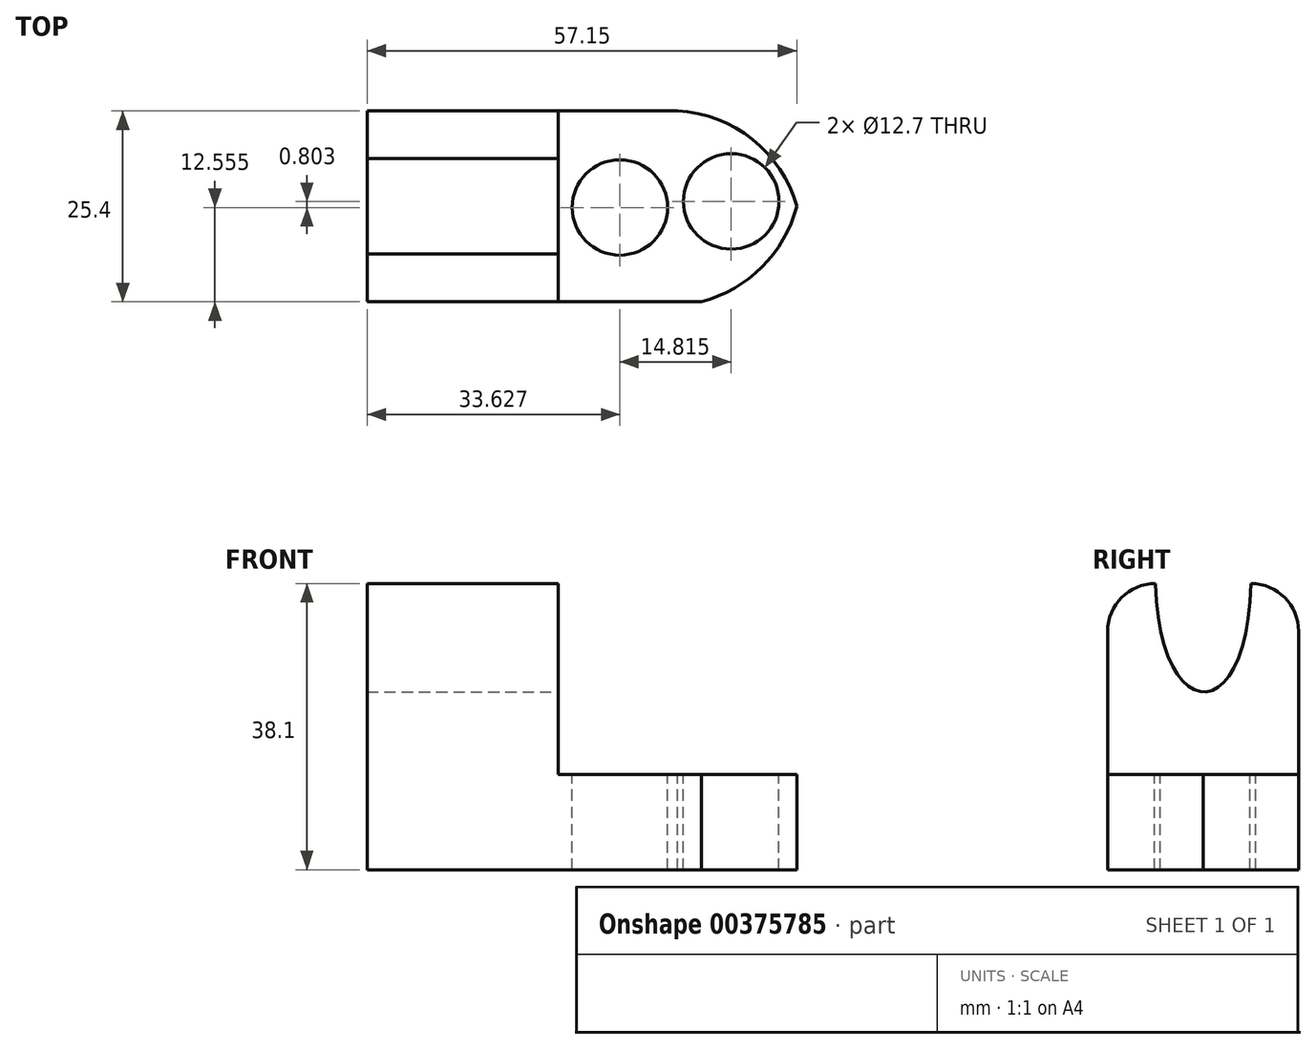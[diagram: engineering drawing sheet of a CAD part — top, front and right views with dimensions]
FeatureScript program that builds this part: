
annotation { "Feature Type Name" : "Feature", "Feature Type Description" : "" }
export const myFeature = defineFeature(function(context is Context, id is Id, definition is map)
    precondition{}
    {
        {
            var Q0;
            Q0=qCreatedBy(makeId("Front.planeOp"),FACE);
            var sketch = newSketch(context, id + "F0", { "sketchPlane" : qUnion([Q0])});
            skLineSegment(sketch, "E0", {"start": v(-57.15, 38.1) * mm, "end": v(-57.15, 0) * mm});
            skLineSegment(sketch, "E1", {"start": v(-57.15, 0) * mm, "end": v(0, 0) * mm});
            skLineSegment(sketch, "E2", {"start": v(0, 0) * mm, "end": v(0, 12.7) * mm});
            skLineSegment(sketch, "E3", {"start": v(0, 12.7) * mm, "end": v(-31.75, 12.7) * mm});
            skLineSegment(sketch, "E4", {"start": v(-31.75, 12.7) * mm, "end": v(-31.75, 38.1) * mm});
            skLineSegment(sketch, "E5", {"start": v(-31.75, 38.1) * mm, "end": v(-57.15, 38.1) * mm});
            skSolve(sketch);
        }
        {
            var Q0;
            Q0=makeQuery(id+"F0.imprint","IMPRINT",FACE,{"disambiguationData":[TD([[makeQuery(id+"F0.imprint","IMPRINT",EDGE,{"derivedFrom":sQuery(id+"F0.wireOp",EDGE,"E0")}),1.0]])]});
            extrude(context, id + "F1", {"entities" : qUnion([Q0]), "depth" : 25.4 * mm});
        }
        {
            var Q0;
            Q0=makeQuery(id+"F1.opExtrude","SWEPT_FACE",FACE,{"disambiguationData":[OSD([sQuery(id+"F0.wireOp",EDGE,"E4")])]});
            var sketch = newSketch(context, id + "F2", { "sketchPlane" : qUnion([Q0])});
            skFitSpline(sketch, "E6", {"points": [v(-19.05, 38.1) * mm, v(-6.35, 38.1) * mm], "startDerivative": vector(1.44, -56.27) * mm, "endDerivative": vector(1.38, 59.05) * mm});
            skLineSegment(sketch, "E7", {"start": v(-19.05, 38.1) * mm, "end": v(-6.35, 38.1) * mm});
            skSolve(sketch);
        }
        {
            var Q0;
            Q0=makeQuery(id+"F2.imprint","IMPRINT",FACE,{"disambiguationData":[TD([[makeQuery(id+"F2.imprint","IMPRINT",EDGE,{"derivedFrom":sQuery(id+"F2.wireOp",EDGE,"E6")}),1.0]])]});
            extrude(context, id + "F3", {"entities" : qUnion([Q0]), "operationType" : NewBodyOperationType.REMOVE, "oppositeDirection" : true, "depth" : 25.4 * mm});
        }
        {
            var Q0;
            Q0=makeQuery(id+"F1.opExtrude","SWEPT_FACE",FACE,{"disambiguationData":[OSD([sQuery(id+"F0.wireOp",EDGE,"E3")])]});
            var sketch = newSketch(context, id + "F4", { "sketchPlane" : qUnion([Q0])});
            skArc(sketch, "E8", {"start": v(0, -12.7) * mm, "mid": v(-5.89, -3.79) * mm, "end": v(-15.88, 0) * mm});
            skArc(sketch, "E9", {"start": v(-12.7, -25.4) * mm, "mid": v(-4.63, -20.77) * mm, "end": v(0, -12.7) * mm});
            skLineSegment(sketch, "E10", {"start": v(-15.88, 0) * mm, "end": v(0, 0) * mm});
            skLineSegment(sketch, "E11", {"start": v(0, 0) * mm, "end": v(0, -12.7) * mm});
            skLineSegment(sketch, "E12", {"start": v(-12.7, -25.4) * mm, "end": v(0, -25.4) * mm});
            skLineSegment(sketch, "E13", {"start": v(0, -25.4) * mm, "end": v(0, -12.7) * mm});
            skSolve(sketch);
        }
        {
            var Q0;
            Q0=makeQuery(id+"F4.imprint","IMPRINT",FACE,{"disambiguationData":[TD([[makeQuery(id+"F4.imprint","IMPRINT",EDGE,{"derivedFrom":sQuery(id+"F4.wireOp",EDGE,"E9")}),-1.0]])]});
            var Q1;
            Q1=makeQuery(id+"F4.imprint","IMPRINT",FACE,{"disambiguationData":[TD([[makeQuery(id+"F4.imprint","IMPRINT",EDGE,{"derivedFrom":sQuery(id+"F4.wireOp",EDGE,"E8")}),-1.0]])]});
            extrude(context, id + "F5", {"entities" : qUnion([Q0, Q1]), "operationType" : NewBodyOperationType.REMOVE, "oppositeDirection" : true, "depth" : 25.4 * mm});
        }
        {
            var Q0;
            Q0=makeQuery(id+"F1.opExtrude","SWEPT_FACE",FACE,{"disambiguationData":[OSD([sQuery(id+"F0.wireOp",EDGE,"E3")])]});
            var sketch = newSketch(context, id + "F6", { "sketchPlane" : qUnion([Q0])});
            skCircle(sketch, "E14", {"center": v(-23.52, -12.84) * mm, "radius": 6.35 * mm});
            skCircle(sketch, "E15", {"center": v(-8.7, -12.04) * mm, "radius": 6.35 * mm});
            skSolve(sketch);
        }
        {
            var Q0;
            Q0=makeQuery(id+"F6.imprint","IMPRINT",FACE,{"disambiguationData":[TD([[makeQuery(id+"F6.imprint","IMPRINT",EDGE,{"derivedFrom":sQuery(id+"F6.wireOp",EDGE,"E14")}),1.0]])]});
            var Q1;
            Q1=makeQuery(id+"F6.imprint","IMPRINT",FACE,{"disambiguationData":[TD([[makeQuery(id+"F6.imprint","IMPRINT",EDGE,{"derivedFrom":sQuery(id+"F6.wireOp",EDGE,"E15")}),1.0]])]});
            extrude(context, id + "F7", {"entities" : qUnion([Q0, Q1]), "operationType" : NewBodyOperationType.REMOVE, "oppositeDirection" : true, "depth" : 25.4 * mm});
        }
        {
            var Q0;
            Q0=makeQuery(id+"F1.opExtrude","SWEPT_FACE",FACE,{"disambiguationData":[OSD([sQuery(id+"F0.wireOp",EDGE,"E0")])]});
            var sketch = newSketch(context, id + "F8", { "sketchPlane" : qUnion([Q0])});
            skArc(sketch, "E16", {"start": v(6.35, 38.1) * mm, "mid": v(1.86, 36.24) * mm, "end": v(0, 31.75) * mm});
            skArc(sketch, "E17", {"start": v(25.4, 31.75) * mm, "mid": v(23.54, 36.24) * mm, "end": v(19.05, 38.1) * mm});
            skLineSegment(sketch, "E18", {"start": v(0, 31.75) * mm, "end": v(0, 38.1) * mm});
            skLineSegment(sketch, "E19", {"start": v(0, 38.1) * mm, "end": v(6.35, 38.1) * mm});
            skLineSegment(sketch, "E20", {"start": v(19.05, 38.1) * mm, "end": v(25.4, 38.1) * mm});
            skLineSegment(sketch, "E21", {"start": v(25.4, 38.1) * mm, "end": v(25.4, 31.75) * mm});
            skSolve(sketch);
        }
        {
            var Q0;
            Q0=makeQuery(id+"F8.imprint","IMPRINT",FACE,{"disambiguationData":[TD([[makeQuery(id+"F8.imprint","IMPRINT",EDGE,{"derivedFrom":sQuery(id+"F8.wireOp",EDGE,"E17")}),-1.0]])]});
            var Q1;
            Q1=makeQuery(id+"F8.imprint","IMPRINT",FACE,{"disambiguationData":[TD([[makeQuery(id+"F8.imprint","IMPRINT",EDGE,{"derivedFrom":sQuery(id+"F8.wireOp",EDGE,"E16")}),-1.0]])]});
            extrude(context, id + "F9", {"entities" : qUnion([Q0, Q1]), "operationType" : NewBodyOperationType.REMOVE, "oppositeDirection" : true, "depth" : 25.4 * mm});
        }
    });
